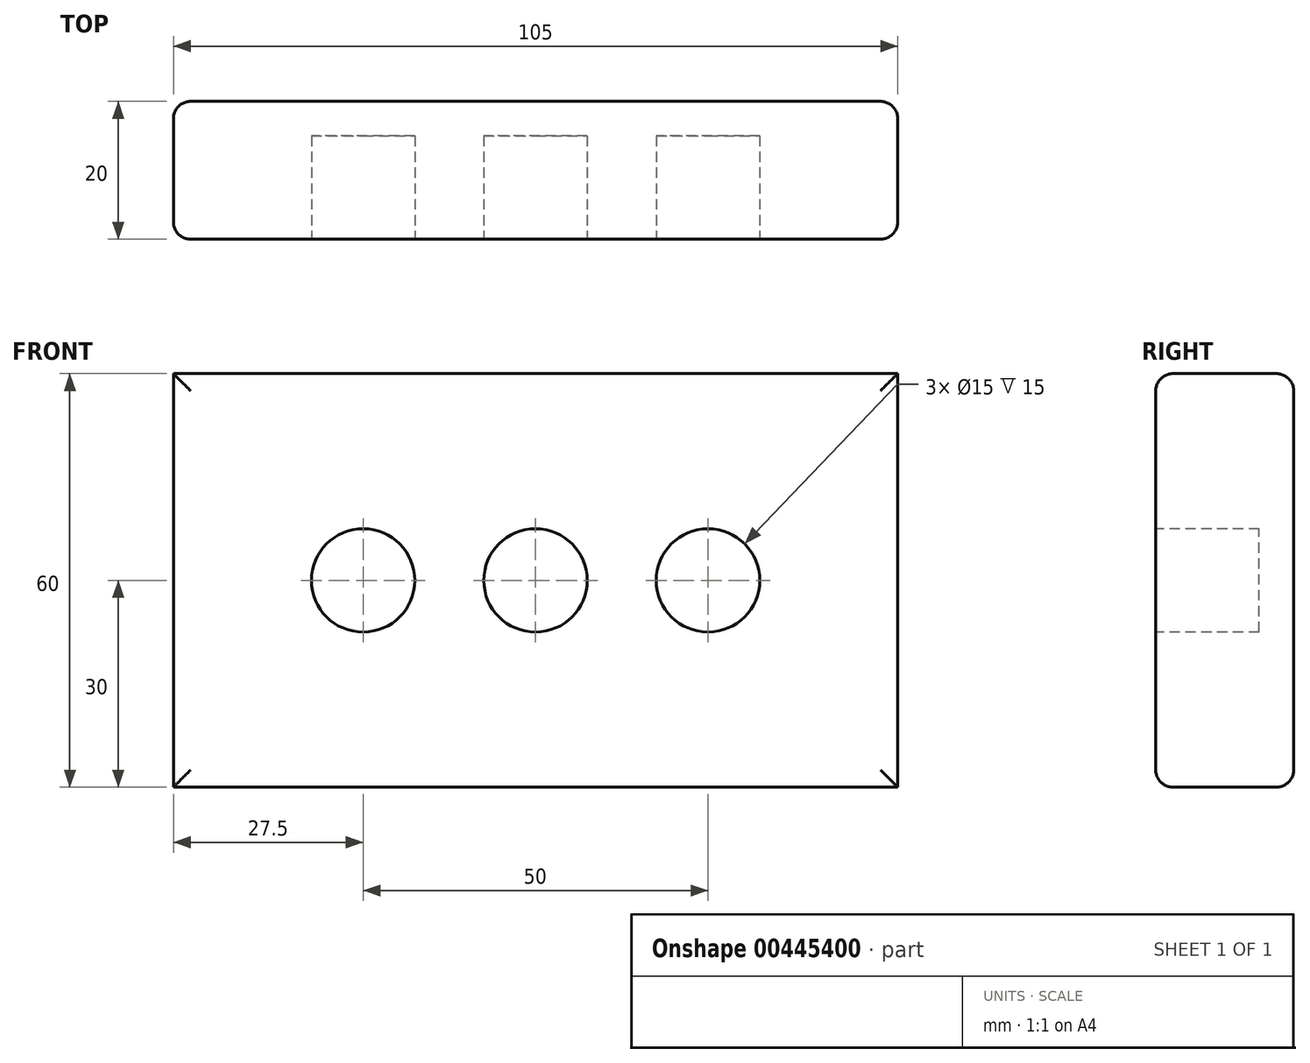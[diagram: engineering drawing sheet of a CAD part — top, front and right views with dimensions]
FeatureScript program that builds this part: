
annotation { "Feature Type Name" : "Feature", "Feature Type Description" : "" }
export const myFeature = defineFeature(function(context is Context, id is Id, definition is map)
    precondition{}
    {
        {
            var Q0;
            Q0=qCreatedBy(makeId("Front.planeOp"),FACE);
            var sketch = newSketch(context, id + "F0", { "sketchPlane" : qUnion([Q0])});
            skLineSegment(sketch, "E0.bottom", {"start": v(52.5, 30) * mm, "end": v(-52.5, 30) * mm});
            skLineSegment(sketch, "E0.top", {"start": v(52.5, -30) * mm, "end": v(-52.5, -30) * mm});
            skLineSegment(sketch, "E0.left", {"start": v(52.5, 30) * mm, "end": v(52.5, -30) * mm});
            skLineSegment(sketch, "E0.right", {"start": v(-52.5, 30) * mm, "end": v(-52.5, -30) * mm});
            skPoint(sketch, "E0.middle", {"position": v(0, 0) * mm});
            skSolve(sketch);
        }
        {
            var Q0;
            Q0 = qSketchRegion(id + "F0", true);
            extrude(context, id + "F1", {"entities" : qUnion([Q0]), "depth" : 20 * mm});
        }
        {
            var Q0;
            Q0=makeQuery(id+"F1.opExtrude","CAP_FACE",FACE,{"disambiguationData":[OSD([sQuery(id+"F0.wireOp",EDGE,"E0.bottom"),sQuery(id+"F0.wireOp",EDGE,"E0.top"),sQuery(id+"F0.wireOp",EDGE,"E0.left"),sQuery(id+"F0.wireOp",EDGE,"E0.right")])],"isStart":false});
            var sketch = newSketch(context, id + "F2", { "sketchPlane" : qUnion([Q0])});
            skCircle(sketch, "E1", {"center": v(0, 0) * mm, "radius": 7.5 * mm});
            skLineSegment(sketch, "E2", {"start": v(7.5, 0) * mm, "end": v(25, 0) * mm});
            skLineSegment(sketch, "E3", {"start": v(-7.5, 0) * mm, "end": v(-25, 0) * mm});
            skCircle(sketch, "E4", {"center": v(-25, 0) * mm, "radius": 7.5 * mm});
            skCircle(sketch, "E5", {"center": v(25, 0) * mm, "radius": 7.5 * mm});
            skSolve(sketch);
        }
        {
            var Q0;
            Q0 = qSketchRegion(id + "F2", true);
            extrude(context, id + "F3", {"entities" : qUnion([Q0]), "operationType" : NewBodyOperationType.REMOVE, "oppositeDirection" : true, "depth" : 15 * mm});
        }
        {
            var Q0;
            Q0=makeQuery(id+"F1.opExtrude","CAP_EDGE",EDGE,{"disambiguationData":[OSD([sQuery(id+"F0.wireOp",EDGE,"E0.right")])],"isStart":false});
            var Q1;
            Q1=makeQuery(id+"F1.opExtrude","CAP_EDGE",EDGE,{"disambiguationData":[OSD([sQuery(id+"F0.wireOp",EDGE,"E0.top")])],"isStart":false});
            var Q2;
            Q2=makeQuery(id+"F1.opExtrude","CAP_EDGE",EDGE,{"disambiguationData":[OSD([sQuery(id+"F0.wireOp",EDGE,"E0.left")])],"isStart":false});
            var Q3;
            Q3=makeQuery(id+"F1.opExtrude","CAP_EDGE",EDGE,{"disambiguationData":[OSD([sQuery(id+"F0.wireOp",EDGE,"E0.bottom")])],"isStart":false});
            var Q4;
            Q4=makeQuery(id+"F1.opExtrude","CAP_EDGE",EDGE,{"disambiguationData":[OSD([sQuery(id+"F0.wireOp",EDGE,"E0.right")])],"isStart":true});
            var Q5;
            Q5=makeQuery(id+"F1.opExtrude","CAP_EDGE",EDGE,{"disambiguationData":[OSD([sQuery(id+"F0.wireOp",EDGE,"E0.bottom")])],"isStart":true});
            var Q6;
            Q6=makeQuery(id+"F1.opExtrude","CAP_EDGE",EDGE,{"disambiguationData":[OSD([sQuery(id+"F0.wireOp",EDGE,"E0.left")])],"isStart":true});
            var Q7;
            Q7=makeQuery(id+"F1.opExtrude","CAP_EDGE",EDGE,{"disambiguationData":[OSD([sQuery(id+"F0.wireOp",EDGE,"E0.top")])],"isStart":true});
            fillet(context, id + "F4", {"entities" : qUnion([Q0, Q1, Q2, Q3, Q4, Q5, Q6, Q7]), "radius" : 2.5 * mm, "tangentPropagation" : true, "allowEdgeOverflow" : false});
        }
    });
